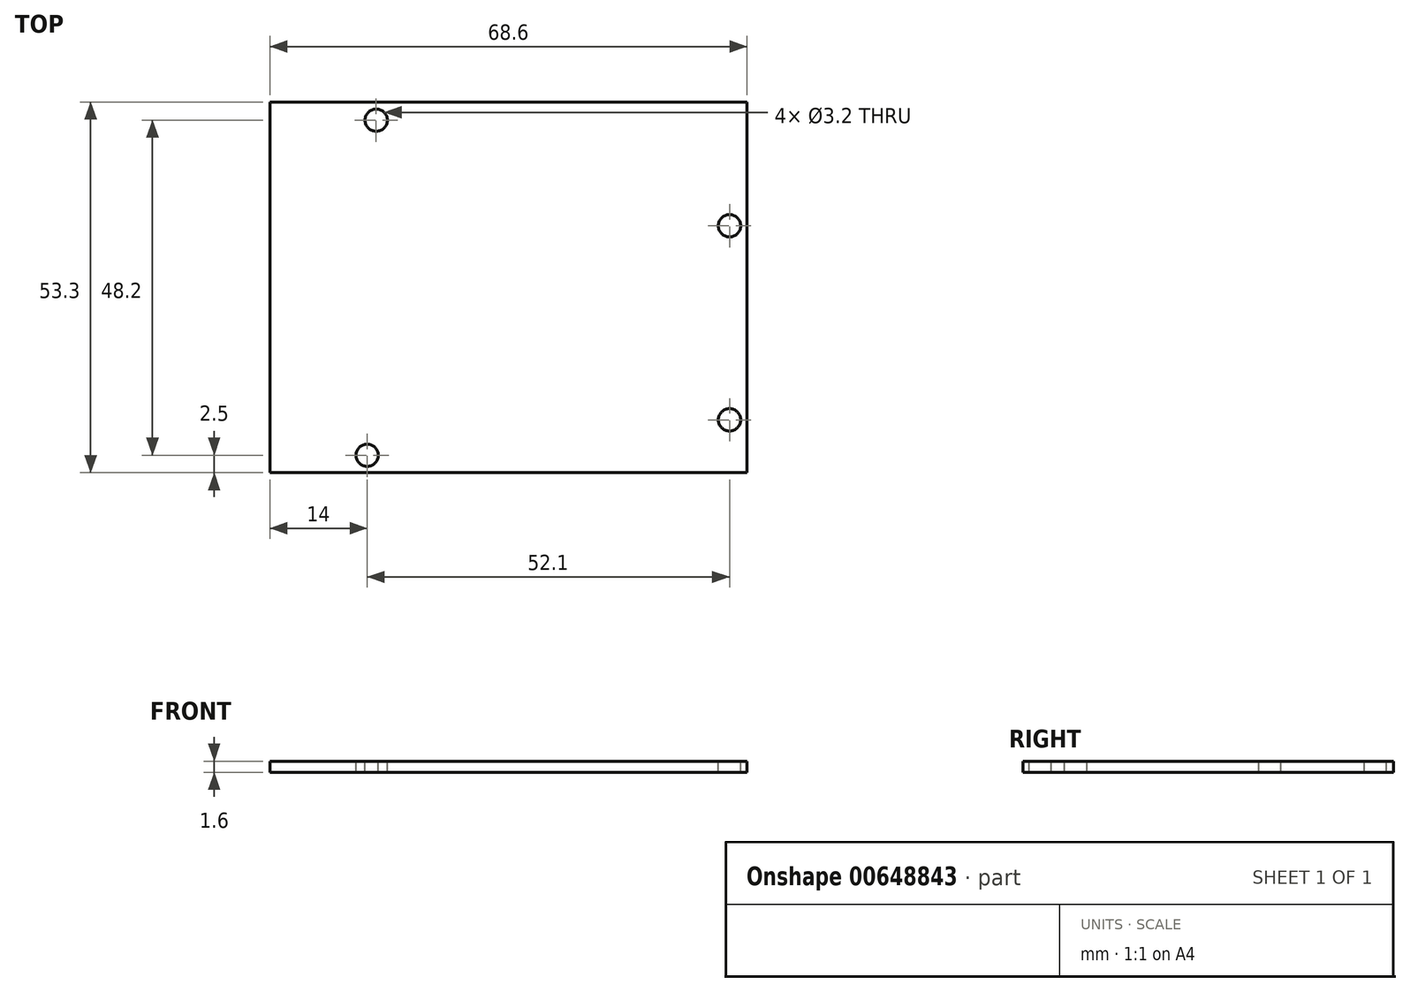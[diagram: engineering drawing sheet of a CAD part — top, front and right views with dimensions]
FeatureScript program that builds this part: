
annotation { "Feature Type Name" : "Feature", "Feature Type Description" : "" }
export const myFeature = defineFeature(function(context is Context, id is Id, definition is map)
    precondition{}
    {
        {
            var Q0;
            Q0=qCreatedBy(makeId("Top.planeOp"),FACE);
            var sketch = newSketch(context, id + "F0", { "sketchPlane" : qUnion([Q0])});
            skLineSegment(sketch, "E0.bottom", {"start": v(0, 0) * mm, "end": v(68.6, 0) * mm});
            skLineSegment(sketch, "E0.top", {"start": v(0, 53.3) * mm, "end": v(68.6, 53.3) * mm});
            skLineSegment(sketch, "E0.left", {"start": v(0, 0) * mm, "end": v(0, 53.3) * mm});
            skLineSegment(sketch, "E0.right", {"start": v(68.6, 0) * mm, "end": v(68.6, 53.3) * mm});
            skPoint(sketch, "E1", {"position": v(15.3, 50.7) * mm});
            skPoint(sketch, "E2", {"position": v(14, 2.5) * mm});
            skPoint(sketch, "E3", {"position": v(66.1, 35.5) * mm});
            skPoint(sketch, "E4", {"position": v(66.1, 7.6) * mm});
            skSolve(sketch);
        }
        {
            var Q0;
            Q0=makeQuery(id+"F0.imprint","IMPRINT",FACE,{"disambiguationData":[TD([[makeQuery(id+"F0.imprint","IMPRINT",EDGE,{"derivedFrom":sQuery(id+"F0.wireOp",EDGE,"E0.bottom")}),1.0]])]});
            extrude(context, id + "F1", {"entities" : qUnion([Q0]), "depth" : 1.6 * mm, "offsetDistance" : 25 * mm});
        }
        {
            var Q0;
            Q0=sQuery(id+"F0.wireOp",VERTEX,"E1");
            var Q1;
            Q1=sQuery(id+"F0.wireOp",VERTEX,"E3");
            var Q2;
            Q2=sQuery(id+"F0.wireOp",VERTEX,"E4");
            var Q3;
            Q3=sQuery(id+"F0.wireOp",VERTEX,"E2");
            var Q4;
            Q4=makeQuery(id+"F1.opExtrude","SWEPT_BODY",BODY,{"disambiguationData":[OSD([sQuery(id+"F0.wireOp",EDGE,"E0.bottom"),sQuery(id+"F0.wireOp",EDGE,"E0.top"),sQuery(id+"F0.wireOp",EDGE,"E0.left"),sQuery(id+"F0.wireOp",EDGE,"E0.right")])]});
            hole(context, id + "F2", {"style" : HoleStyle.SIMPLE, "endStyle" : HoleEndStyle.THROUGH, "oppositeDirection" : true, "holeDiameter" : 3.2 * mm, "majorDiameter" : 5 * mm, "tappedDepth" : 12 * mm, "tapClearance" : 3, "locations" : qUnion([Q0, Q1, Q2, Q3]), "scope" : qUnion([Q4])});
        }
    });
